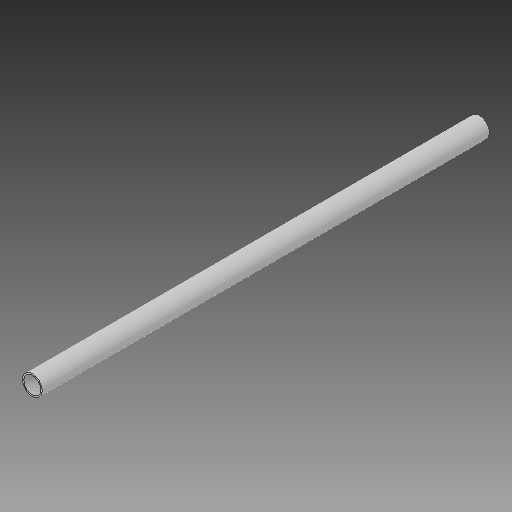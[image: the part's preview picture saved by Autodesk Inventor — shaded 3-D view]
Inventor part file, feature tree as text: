
AUTODESK INVENTOR PART (.ipt)
format: ipt  version: 2018.3 (Build 223284000, 284)  size: 80,896 bytes
history: native  units: mm
features: other x1, extrude x1, sketch x1
ambient origin geometry x8: Origin, YZ Plane, XZ Plane, XY Plane, X Axis, Y Axis, Z Axis, Center Point
bodies: Body1 (feature_tree)
feature tree (3):
  other  "ソリッド1"
  extrude  "押し出し1"  Depth=16.0mm
  sketch  "スケッチ1"
